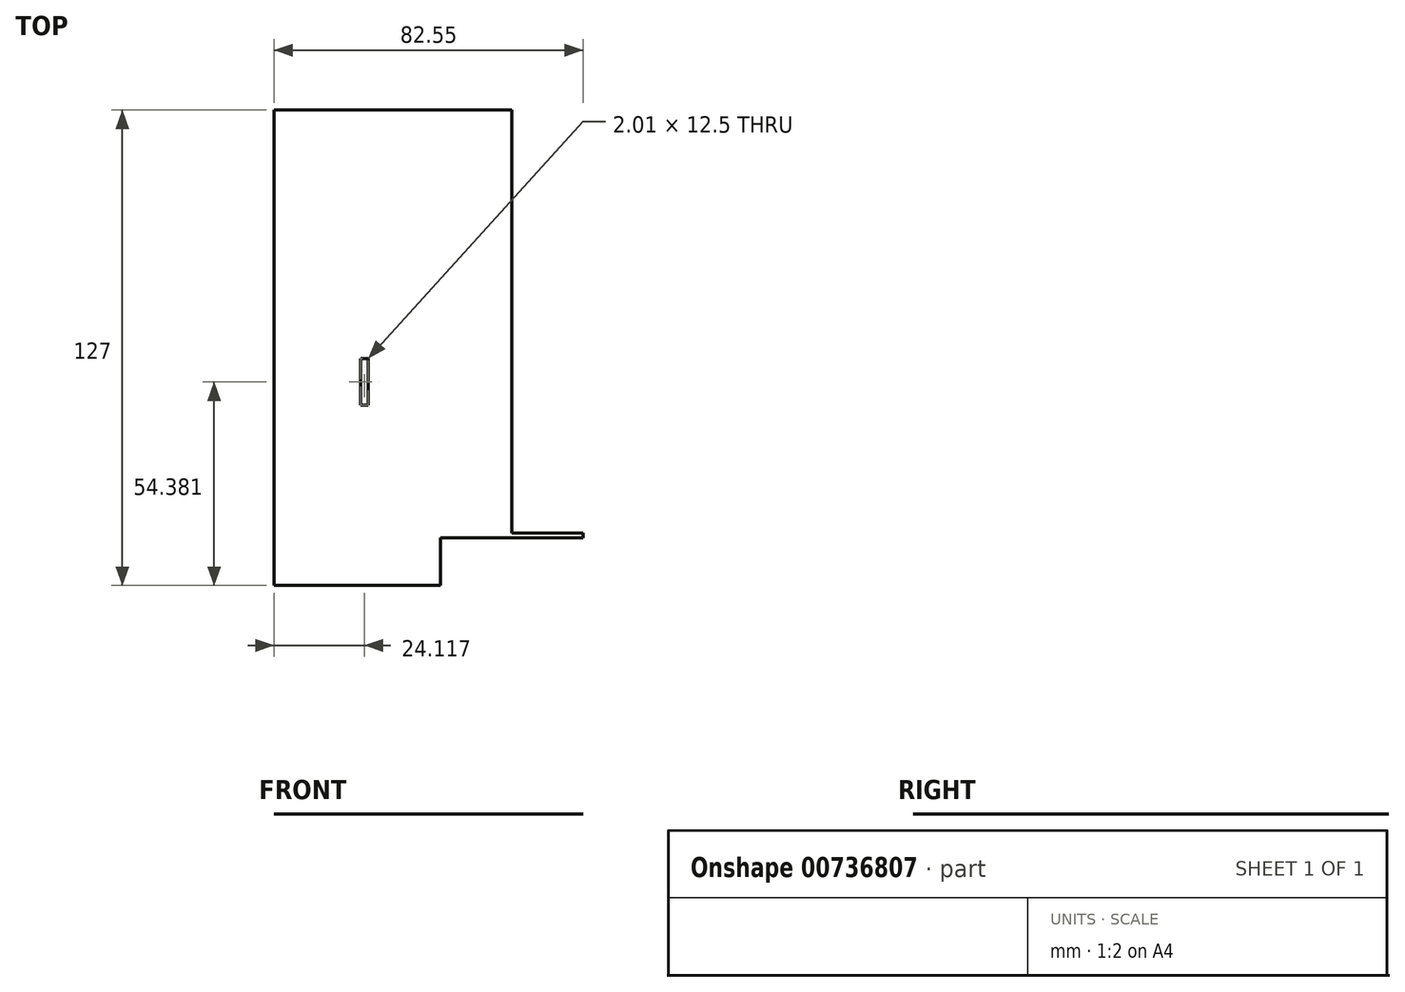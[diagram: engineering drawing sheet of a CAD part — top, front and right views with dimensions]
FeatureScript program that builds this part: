
annotation { "Feature Type Name" : "Feature", "Feature Type Description" : "" }
export const myFeature = defineFeature(function(context is Context, id is Id, definition is map)
    precondition{}
    {
        {
            var Q0;
            Q0=qCreatedBy(makeId("Top.planeOp"),FACE);
            var sketch = newSketch(context, id + "F0", { "sketchPlane" : qUnion([Q0])});
            skLineSegment(sketch, "E0.bottom", {"start": v(0, 0) * mm, "end": v(-127, 0) * mm});
            skLineSegment(sketch, "E0.top", {"start": v(0, 127) * mm, "end": v(-127, 127) * mm});
            skLineSegment(sketch, "E0.left", {"start": v(0, 0) * mm, "end": v(0, 127) * mm});
            skLineSegment(sketch, "E0.right", {"start": v(-127, 0) * mm, "end": v(-127, 127) * mm});
            skLineSegment(sketch, "E1.bottom", {"start": v(-127, 127) * mm, "end": v(-63.5, 127) * mm});
            skLineSegment(sketch, "E1.top", {"start": v(-82.55, 0) * mm, "end": v(-63.5, 0) * mm});
            skLineSegment(sketch, "E1.left", {"start": v(-127, 127) * mm, "end": v(-127, 0) * mm});
            skLineSegment(sketch, "E2.bottom", {"start": v(0, 127) * mm, "end": v(0, 127) * mm});
            skLineSegment(sketch, "E2.top", {"start": v(0, 0) * mm, "end": v(0, 0) * mm});
            skLineSegment(sketch, "E2.left", {"start": v(0, 127) * mm, "end": v(0, 0) * mm});
            skLineSegment(sketch, "E3", {"start": v(-63.5, 0) * mm, "end": v(-63.5, 127) * mm});
            skLineSegment(sketch, "E4", {"start": v(-127, 0) * mm, "end": v(-127, 54.38) * mm});
            skLineSegment(sketch, "E5", {"start": v(-127, 54.38) * mm, "end": v(-103.89, 54.38) * mm});
            skLineSegment(sketch, "E6.bottom", {"start": v(-103.89, 48.13) * mm, "end": v(-101.88, 48.13) * mm});
            skLineSegment(sketch, "E6.top", {"start": v(-103.89, 60.63) * mm, "end": v(-101.88, 60.63) * mm});
            skLineSegment(sketch, "E6.left", {"start": v(-103.89, 48.13) * mm, "end": v(-103.89, 60.63) * mm});
            skLineSegment(sketch, "E6.right", {"start": v(-101.88, 48.13) * mm, "end": v(-101.88, 60.63) * mm});
            skLineSegment(sketch, "E7.MirrorCS", {"start": v(-25.12, 48.13) * mm, "end": v(-25.12, 60.63) * mm});
            skLineSegment(sketch, "E8.MirrorCS", {"start": v(-23.11, 60.63) * mm, "end": v(-25.12, 60.63) * mm});
            skLineSegment(sketch, "E9.MirrorCS", {"start": v(-23.11, 48.13) * mm, "end": v(-25.12, 48.13) * mm});
            skLineSegment(sketch, "E10.MirrorCS", {"start": v(-23.11, 48.13) * mm, "end": v(-23.11, 60.63) * mm});
            skLineSegment(sketch, "E11", {"start": v(-127, 0) * mm, "end": v(-95.25, 0) * mm});
            skLineSegment(sketch, "E12", {"start": v(-82.55, 0) * mm, "end": v(-82.55, 12.7) * mm});
            skLineSegment(sketch, "E13", {"start": v(-82.55, 12.7) * mm, "end": v(-44.45, 12.7) * mm});
            skLineSegment(sketch, "E14", {"start": v(-82.55, 12.7) * mm, "end": v(-82.55, 13.97) * mm});
            skLineSegment(sketch, "E15", {"start": v(-82.55, 13.97) * mm, "end": v(-44.45, 13.97) * mm});
            skLineSegment(sketch, "E16", {"start": v(-44.45, 13.97) * mm, "end": v(-44.45, 12.7) * mm});
            skSolve(sketch);
        }
        {
            var Q0;
            Q0=makeQuery(id+"F0.imprint","IMPRINT",FACE,{"disambiguationData":[TD([[makeQuery(id+"F0.imprint","IMPRINT",EDGE,{"derivedFrom":sQuery(id+"F0.wireOp",EDGE,"E0.bottom")}),-1.0]])]});
            var Q1;
            Q1=makeQuery(id+"F0.imprint","IMPRINT",FACE,{"disambiguationData":[TD([[makeQuery(id+"F0.imprint","IMPRINT",EDGE,{"derivedFrom":sQuery(id+"F0.wireOp",EDGE,"E1.bottom")}),-1.0]])]});
            var Q2;
            {var subQ0=sQuery(id+"F0.wireOp",EDGE,"E1.top");Q2=makeQuery(id+"F0.imprint","IMPRINT",FACE,{"disambiguationData":[TD([[makeQuery(id+"F0.imprint","IMPRINT",EDGE,{"derivedFrom":subQ0}),1.0]])]});}
            var Q3;
            {var subQ5=sQuery(id+"F0.wireOp",EDGE,"E14");Q3=makeQuery(id+"F0.imprint","IMPRINT",FACE,{"disambiguationData":[TD([[makeQuery(id+"F0.imprint","IMPRINT",EDGE,{"derivedFrom":subQ5}),-1.0]])]});}
            var Q4;
            {var subQ5=sQuery(id+"F0.wireOp",EDGE,"E16");Q4=makeQuery(id+"F0.imprint","IMPRINT",FACE,{"disambiguationData":[TD([[makeQuery(id+"F0.imprint","IMPRINT",EDGE,{"derivedFrom":subQ5}),-1.0]])]});}
            extrude(context, id + "F1", {"entities" : qUnion([Q0, Q1, Q2, Q3, Q4]), "depth" : 1 / 203.2 * mm, "offsetDistance" : 25.4 * mm});
        }
    });
